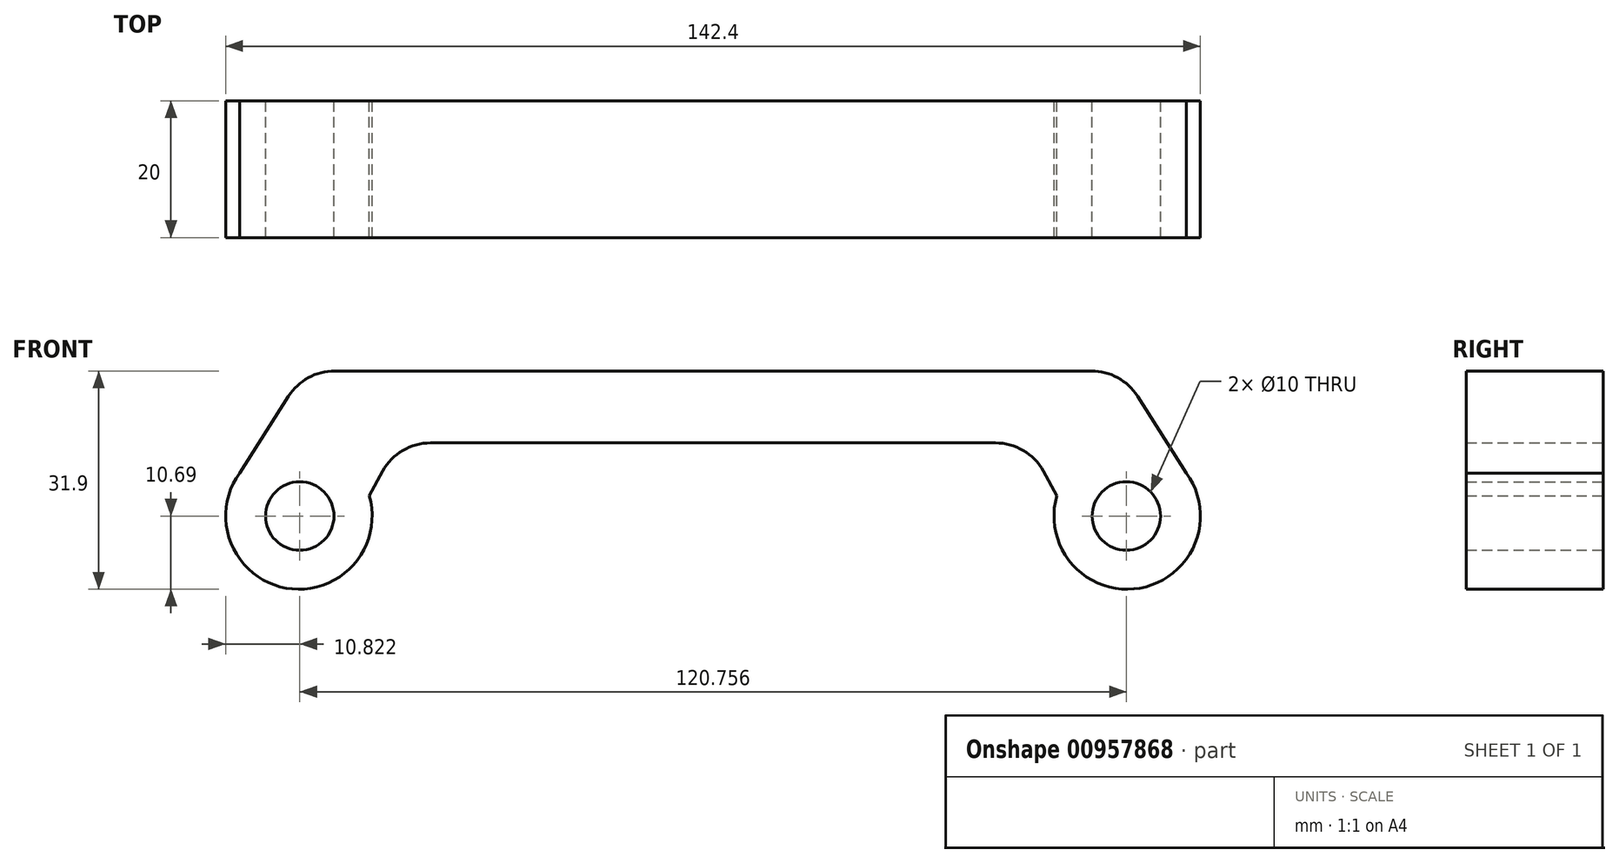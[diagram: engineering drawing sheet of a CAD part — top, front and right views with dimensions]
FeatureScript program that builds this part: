
annotation { "Feature Type Name" : "Feature", "Feature Type Description" : "" }
export const myFeature = defineFeature(function(context is Context, id is Id, definition is map)
    precondition{}
    {
        {
            var Q0;
            Q0=qCreatedBy(makeId("Front.planeOp"),FACE);
            var sketch = newSketch(context, id + "F0", { "sketchPlane" : qUnion([Q0])});
            skCircle(sketch, "E0", {"center": v(-60.5, 0) * mm, "radius": 10.7 * mm});
            skLineSegment(sketch, "E1", {"start": v(-69.15, 6.3) * mm, "end": v(-62.02, 17.5) * mm});
            skLineSegment(sketch, "E2", {"start": v(-55.27, 21.21) * mm, "end": v(0, 21.21) * mm});
            skLineSegment(sketch, "E3", {"start": v(0, 21.21) * mm, "end": v(0, 10.7) * mm});
            skLineSegment(sketch, "E4", {"start": v(0, 10.7) * mm, "end": v(-41.25, 10.7) * mm});
            skLineSegment(sketch, "E5", {"start": v(-48.26, 6.55) * mm, "end": v(-50.23, 2.97) * mm});
            skPoint(sketch, "E6.visualSharp", {"position": v(-59.67, 21.21) * mm});
            skArc(sketch, "E6.filletArc", {"start": v(-55.27, 21.21) * mm, "mid": v(-59.12, 20.22) * mm, "end": v(-62.02, 17.5) * mm});
            skPoint(sketch, "E7.visualSharp", {"position": v(-45.98, 10.7) * mm});
            skArc(sketch, "E7.filletArc", {"start": v(-41.25, 10.7) * mm, "mid": v(-45.32, 9.58) * mm, "end": v(-48.26, 6.55) * mm});
            skSolve(sketch);
        }
        {
            var Q0;
            Q0=makeQuery(id+"F0.imprint","IMPRINT",FACE,{"disambiguationData":[TD([[makeQuery(id+"F0.imprint","IMPRINT",EDGE,{"derivedFrom":sQuery(id+"F0.wireOp",EDGE,"E0")}),1.0]])]});
            extrude(context, id + "F1", {"entities" : qUnion([Q0]), "depth" : 20 * mm, "offsetDistance" : 25 * mm});
        }
        {
            var Q0;
            Q0=makeQuery(id+"F1.opExtrude","CAP_FACE",FACE,{"disambiguationData":[OSD([sQuery(id+"F0.wireOp",EDGE,"E0")])],"isStart":false});
            var sketch = newSketch(context, id + "F2", { "sketchPlane" : qUnion([Q0])});
            skPoint(sketch, "E8", {"position": v(-60.5, 0) * mm});
            skSolve(sketch);
        }
        {
            var Q0;
            Q0=sQuery(id+"F2.wireOp",VERTEX,"E8");
            var Q1;
            Q1=makeQuery(id+"F1.opExtrude","SWEPT_BODY",BODY,{"disambiguationData":[OSD([sQuery(id+"F0.wireOp",EDGE,"E0")])]});
            hole(context, id + "F3", {"style" : HoleStyle.SIMPLE, "endStyle" : HoleEndStyle.THROUGH, "holeDiameter" : 10 * mm, "majorDiameter" : 5 * mm, "isTappedThrough" : true, "tappedDepth" : 12 * mm, "tapClearance" : 3, "locations" : qUnion([Q0]), "scope" : qUnion([Q1])});
        }
        {
            var Q0;
            Q0 = qSketchRegion(id + "F0", true);
            extrude(context, id + "F4", {"entities" : qUnion([Q0]), "operationType" : NewBodyOperationType.ADD, "depth" : 20 * mm, "offsetDistance" : 25 * mm});
        }
        {
            var Q0;
            Q0=qCreatedBy(makeId("Front.planeOp"),FACE);
            var sketch = newSketch(context, id + "F5", { "sketchPlane" : qUnion([Q0])});
            skPoint(sketch, "E9", {"position": v(-60.38, 0) * mm});
            skSolve(sketch);
        }
        {
            var Q0;
            Q0=sQuery(id+"F5.wireOp",VERTEX,"E9");
            var Q1;
            Q1=makeQuery(id+"F1.opExtrude","SWEPT_BODY",BODY,{"disambiguationData":[OSD([sQuery(id+"F0.wireOp",EDGE,"E0")])]});
            hole(context, id + "F6", {"style" : HoleStyle.SIMPLE, "endStyle" : HoleEndStyle.THROUGH, "oppositeDirection" : true, "holeDiameter" : 10 * mm, "majorDiameter" : 5 * mm, "isTappedThrough" : true, "tappedDepth" : 12 * mm, "tapClearance" : 3, "locations" : qUnion([Q0]), "scope" : qUnion([Q1])});
        }
        {
            var Q0;
            Q0=makeQuery(id+"F1.opExtrude","SWEPT_BODY",BODY,{"disambiguationData":[OSD([sQuery(id+"F0.wireOp",EDGE,"E0")])]});
            var Q1;
            Q1=qCreatedBy(makeId("Right.planeOp"),FACE);
            mirror(context, id + "F7", {"operationType" : NewBodyOperationType.ADD, "entities" : qUnion([Q0]), "mirrorPlane" : qUnion([Q1])});
        }
    });
